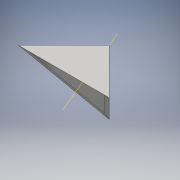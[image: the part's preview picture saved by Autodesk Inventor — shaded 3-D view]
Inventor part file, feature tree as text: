
AUTODESK INVENTOR PART (.ipt)
format: ipt  version: 2016 (Build 200138000, 138)  size: 135,168 bytes
history: native  units: mm
features: sketch x5, other x3, plane x3, extrude x2, projected_geometry x2, pattern_circular x1
ambient origin geometry x8: Origin, YZ Plane, XZ Plane, XY Plane, X Axis, Y Axis, Z Axis, Center Point
bodies: Solid1 (feature_tree)
feature tree (16):
  other  "Table"
  other  "Part2-01"
  extrude  "Extrusion1"  TaperAngle=45.0deg  [1 undecoded]
  sketch  "Sketch4"  dims[d9=82.0mm]
  plane  "Work Plane2"
  sketch  "Sketch5"  dims[d10=3.0mm d11=-7.853982mm d14=30.0mm d15=360.0deg]
  other  "Work Axis2"
  pattern_circular  "Circular Pattern1"  Count=3 Angle=360.0deg
  sketch  "Sketch6"  dims[d18=23.671361mm d20=15.0mm]
  plane  "Work Plane4"
  extrude  "Extrusion2"  Depth=15.0mm
  sketch  "Sketch3"  dims[d7=90.0deg d8=45.0deg]
  projected_geometry  "Projected Loop1"
  plane  "Work Plane3"
  sketch  "Sketch7"  dims[d21=3.0mm d22=0.0mm]
  projected_geometry  "Project Cut Edges1"
note: 1 required parameter value undecoded (feature->parameter linkage not recoverable at this tier; creation-order binding heuristic only, values carry confidence <= 0.55)
